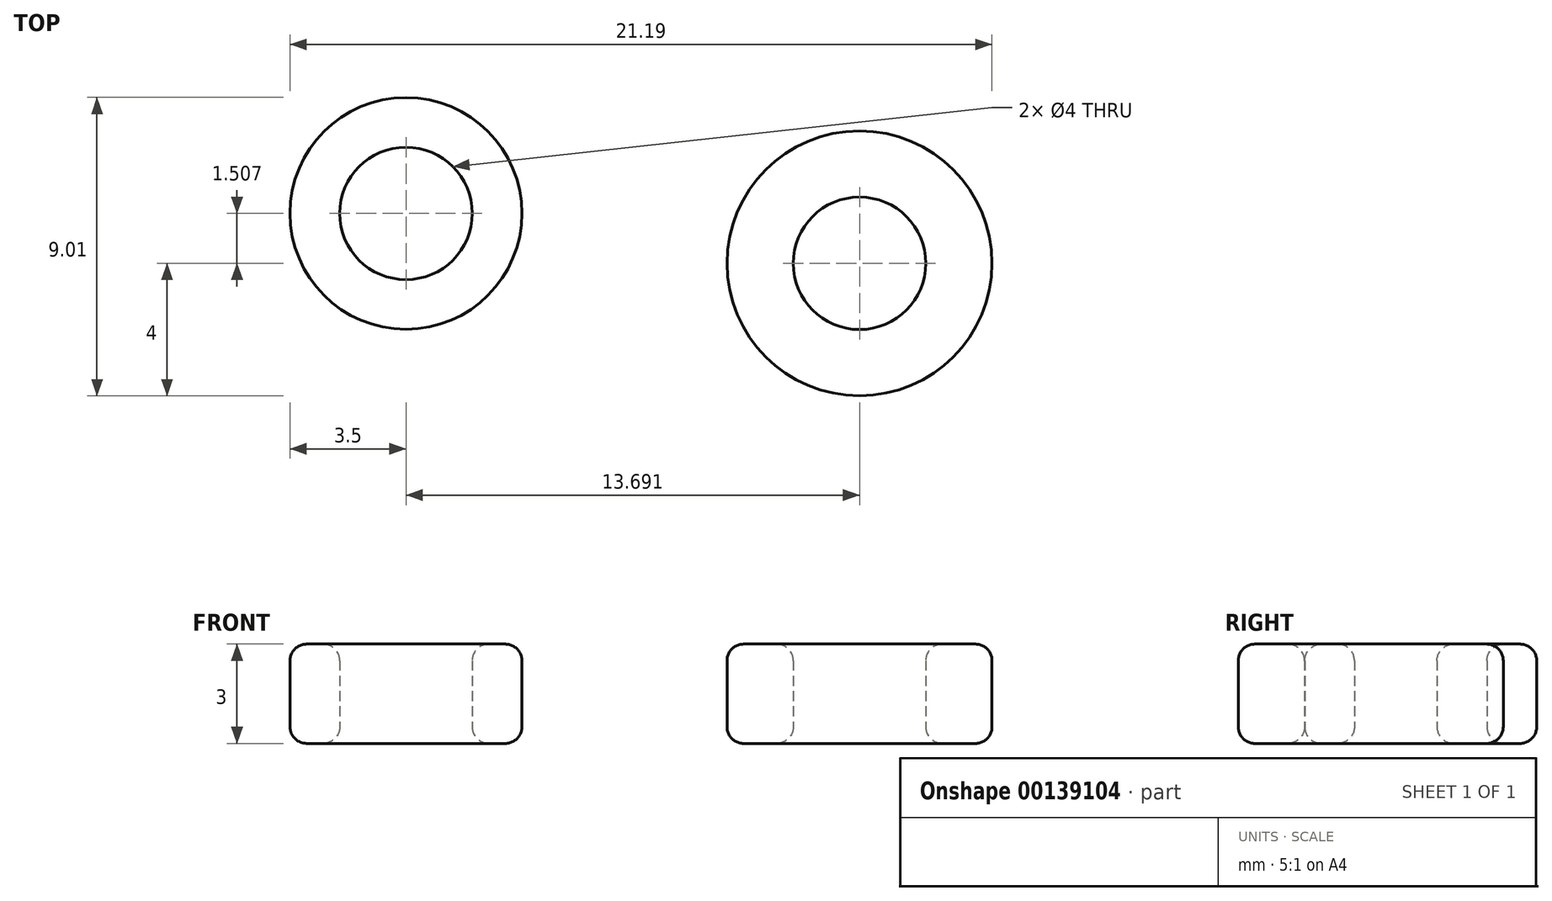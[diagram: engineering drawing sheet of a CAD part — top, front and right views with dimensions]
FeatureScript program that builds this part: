
annotation { "Feature Type Name" : "Feature", "Feature Type Description" : "" }
export const myFeature = defineFeature(function(context is Context, id is Id, definition is map)
    precondition{}
    {
        {
            var Q0;
            Q0=qCreatedBy(makeId("Top.planeOp"),FACE);
            var sketch = newSketch(context, id + "F0", { "sketchPlane" : qUnion([Q0])});
            skCircle(sketch, "E0", {"center": v(0, 0) * mm, "radius": 4 * mm});
            skCircle(sketch, "E1.0", {"center": v(0, 0) * mm, "radius": 2 * mm});
            skCircle(sketch, "E2", {"center": v(-13.7, 1.5) * mm, "radius": 3.5 * mm});
            skCircle(sketch, "E3.0", {"center": v(-13.7, 1.5) * mm, "radius": 2 * mm});
            skSolve(sketch);
        }
        {
            var Q0;
            Q0=makeQuery(id+"F0.imprint","IMPRINT",FACE,{"disambiguationData":[TD([[makeQuery(id+"F0.imprint","IMPRINT",EDGE,{"derivedFrom":sQuery(id+"F0.wireOp",EDGE,"E0")}),1.0]])]});
            extrude(context, id + "F1", {"entities" : qUnion([Q0]), "depth" : 3 * mm});
        }
        {
            var Q0;
            Q0=makeQuery(id+"F1.opExtrude","CAP_EDGE",EDGE,{"disambiguationData":[OSD([sQuery(id+"F0.wireOp",EDGE,"E1.0")])],"isStart":false});
            var Q1;
            Q1=makeQuery(id+"F1.opExtrude","CAP_EDGE",EDGE,{"disambiguationData":[OSD([sQuery(id+"F0.wireOp",EDGE,"E1.0")])],"isStart":true});
            var Q2;
            Q2=makeQuery(id+"F1.opExtrude","CAP_EDGE",EDGE,{"disambiguationData":[OSD([sQuery(id+"F0.wireOp",EDGE,"E0")])],"isStart":true});
            var Q3;
            Q3=makeQuery(id+"F1.opExtrude","CAP_EDGE",EDGE,{"disambiguationData":[OSD([sQuery(id+"F0.wireOp",EDGE,"E0")])],"isStart":false});
            fillet(context, id + "F2", {"entities" : qUnion([Q0, Q1, Q2, Q3]), "radius" : .5 * mm, "tangentPropagation" : true, "allowEdgeOverflow" : false});
        }
        {
            var Q0;
            Q0 = qSketchRegion(id + "F0", true);
            extrude(context, id + "F3", {"entities" : qUnion([Q0]), "operationType" : NewBodyOperationType.ADD, "depth" : 3 * mm});
        }
        {
            var Q0;
            Q0=makeQuery(id+"F3.opExtrude","CAP_EDGE",EDGE,{"disambiguationData":[OSD([sQuery(id+"F0.wireOp",EDGE,"E2")])],"isStart":false});
            var Q1;
            Q1=makeQuery(id+"F3.opExtrude","CAP_EDGE",EDGE,{"disambiguationData":[OSD([sQuery(id+"F0.wireOp",EDGE,"E3.0")])],"isStart":false});
            var Q2;
            Q2=makeQuery(id+"F3.opExtrude","CAP_EDGE",EDGE,{"disambiguationData":[OSD([sQuery(id+"F0.wireOp",EDGE,"E2")])],"isStart":true});
            var Q3;
            Q3=makeQuery(id+"F3.opExtrude","CAP_EDGE",EDGE,{"disambiguationData":[OSD([sQuery(id+"F0.wireOp",EDGE,"E3.0")])],"isStart":true});
            fillet(context, id + "F4", {"entities" : qUnion([Q0, Q1, Q2, Q3]), "radius" : 0.5 * mm, "tangentPropagation" : true, "allowEdgeOverflow" : false});
        }
        {
            var Q0;
            Q0=makeQuery(id+"F3.opExtrude","CAP_EDGE",EDGE,{"disambiguationData":[OSD([sQuery(id+"F0.wireOp",EDGE,"E0")])],"isStart":false});
            var Q1;
            Q1=makeQuery(id+"F3.opExtrude","CAP_EDGE",EDGE,{"disambiguationData":[OSD([sQuery(id+"F0.wireOp",EDGE,"E1.0")])],"isStart":false});
            var Q2;
            Q2=makeQuery(id+"F3.opExtrude","CAP_EDGE",EDGE,{"disambiguationData":[OSD([sQuery(id+"F0.wireOp",EDGE,"E0")])],"isStart":true});
            var Q3;
            Q3=makeQuery(id+"F3.opExtrude","CAP_EDGE",EDGE,{"disambiguationData":[OSD([sQuery(id+"F0.wireOp",EDGE,"E1.0")])],"isStart":true});
            fillet(context, id + "F5", {"entities" : qUnion([Q0, Q1, Q2, Q3]), "radius" : .5 * mm, "tangentPropagation" : true, "allowEdgeOverflow" : false});
        }
    });
